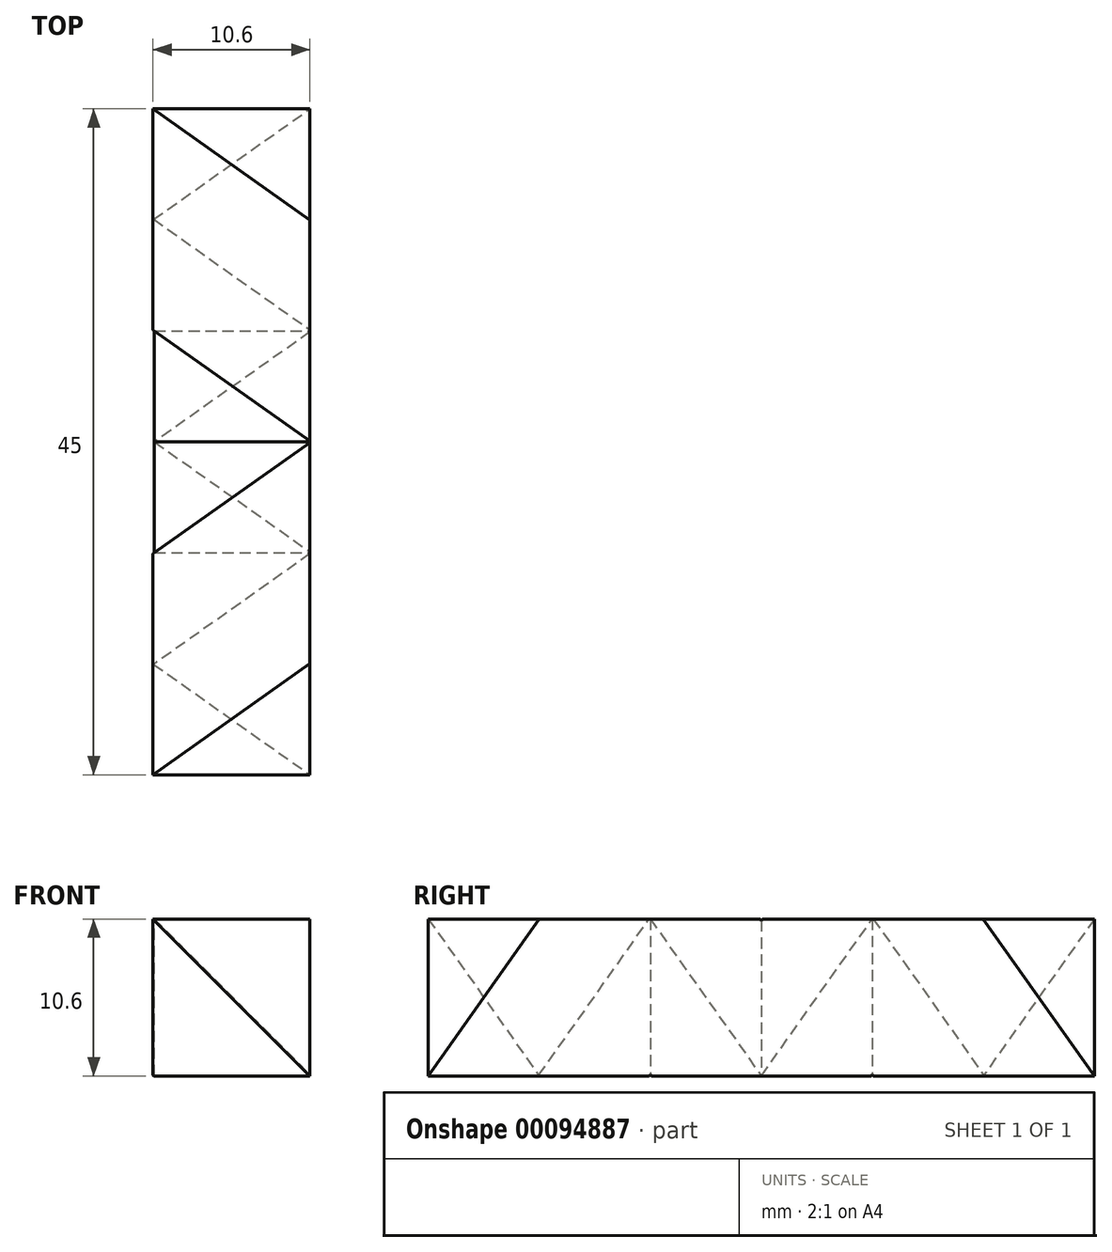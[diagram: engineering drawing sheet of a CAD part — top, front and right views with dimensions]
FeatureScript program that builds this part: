
annotation { "Feature Type Name" : "Feature", "Feature Type Description" : "" }
export const myFeature = defineFeature(function(context is Context, id is Id, definition is map)
    precondition{}
    {
        {
            var Q0;
            Q0=qCreatedBy(makeId("Front.planeOp"),FACE);
            var sketch = newSketch(context, id + "F0", { "sketchPlane" : qUnion([Q0])});
            skLineSegment(sketch, "E0.bottom", {"start": v(5.3, -5.3) * mm, "end": v(-5.3, -5.3) * mm});
            skLineSegment(sketch, "E0.top", {"start": v(5.3, 5.3) * mm, "end": v(-5.3, 5.3) * mm});
            skLineSegment(sketch, "E0.left", {"start": v(5.3, -5.3) * mm, "end": v(5.3, 5.3) * mm});
            skLineSegment(sketch, "E0.right", {"start": v(-5.3, -5.3) * mm, "end": v(-5.3, 5.3) * mm});
            skPoint(sketch, "E0.middle", {"position": v(0, 0) * mm});
            skSolve(sketch);
        }
        {
            var Q0;
            Q0=qSketchRegion(id+"F0",true);
            extrude(context, id + "F1", {"entities" : qUnion([Q0]), "depth" : 45 * mm, "symmetric" : true});
        }
        {
            var Q0;
            Q0=makeQuery(id+"F1.opExtrude","CAP_VERTEX",VERTEX,{"disambiguationData":[OSD([sQuery(id+"F0.wireOp",EDGE,"E0.top"),sQuery(id+"F0.wireOp",EDGE,"E0.left")])],"isStart":false});
            var Q1;
            Q1=makeQuery(id+"F1.opExtrude","CAP_VERTEX",VERTEX,{"disambiguationData":[OSD([sQuery(id+"F0.wireOp",EDGE,"E0.top"),sQuery(id+"F0.wireOp",EDGE,"E0.left")])],"isStart":true});
            var Q2;
            Q2=makeQuery(id+"F1.opExtrude","CAP_VERTEX",VERTEX,{"disambiguationData":[OSD([sQuery(id+"F0.wireOp",EDGE,"E0.bottom"),sQuery(id+"F0.wireOp",EDGE,"E0.right")])],"isStart":true});
            cPlane(context, id + "F2", {"entities" : qUnion([Q0, Q1, Q2]), "cplaneType" : CPlaneType.THREE_POINT, "offset" : 0 * mm, "width" : 150 * mm, "height" : 150 * mm});
        }
        {
            var Q0;
            Q0=qCreatedBy(id+"F2.planeOp",FACE);
            var sketch = newSketch(context, id + "F3", { "sketchPlane" : qUnion([Q0])});
            skLineSegment(sketch, "E1", {"start": v(22.5, 0) * mm, "end": v(15, 7.5) * mm});
            skLineSegment(sketch, "E2", {"start": v(15, -7.5) * mm, "end": v(22.5, 0) * mm});
            skLineSegment(sketch, "E3", {"start": v(15, 7.5) * mm, "end": v(15, 9.5) * mm});
            skLineSegment(sketch, "E4", {"start": v(15, 9.5) * mm, "end": v(24.5, 9.5) * mm});
            skLineSegment(sketch, "E5", {"start": v(24.5, 9.5) * mm, "end": v(24.5, -9.5) * mm});
            skLineSegment(sketch, "E6", {"start": v(24.5, -9.5) * mm, "end": v(15, -9.5) * mm});
            skLineSegment(sketch, "E7", {"start": v(15, -9.5) * mm, "end": v(15, -7.5) * mm});
            skLineSegment(sketch, "E8", {"start": v(0, 16.28) * mm, "end": v(0, -17.75) * mm, "construction": true});
            skLineSegment(sketch, "E9.MirrorCS", {"start": v(-22.5, 0) * mm, "end": v(-15, 7.5) * mm});
            skLineSegment(sketch, "E10.MirrorCS", {"start": v(-15, 7.5) * mm, "end": v(-15, 9.5) * mm});
            skLineSegment(sketch, "E11.MirrorCS", {"start": v(-15, 9.5) * mm, "end": v(-24.5, 9.5) * mm});
            skLineSegment(sketch, "E12.MirrorCS", {"start": v(-24.5, 9.5) * mm, "end": v(-24.5, -9.5) * mm});
            skLineSegment(sketch, "E13.MirrorCS", {"start": v(-24.5, -9.5) * mm, "end": v(-15, -9.5) * mm});
            skLineSegment(sketch, "E14.MirrorCS", {"start": v(-15, -9.5) * mm, "end": v(-15, -7.5) * mm});
            skLineSegment(sketch, "E15.MirrorCS", {"start": v(-15, -7.5) * mm, "end": v(-22.5, 0) * mm});
            skSolve(sketch);
        }
        {
            var Q0;
            Q0=makeQuery(id+"F3.imprint","IMPRINT",FACE,{"disambiguationData":[TD([[makeQuery(id+"F3.imprint","IMPRINT",EDGE,{"derivedFrom":sQuery(id+"F3.wireOp",EDGE,"E9.MirrorCS")}),1.0]])]});
            var Q1;
            Q1=makeQuery(id+"F3.imprint","IMPRINT",FACE,{"disambiguationData":[TD([[makeQuery(id+"F3.imprint","IMPRINT",EDGE,{"derivedFrom":sQuery(id+"F3.wireOp",EDGE,"E1")}),-1.0]])]});
            extrude(context, id + "F4", {"entities" : qUnion([Q0, Q1]), "operationType" : NewBodyOperationType.REMOVE, "oppositeDirection" : true, "depth" : 30 * mm, "symmetric" : true});
        }
        {
            var Q0;
            Q0=qCreatedBy(id+"F2.planeOp",FACE);
            var sketch = newSketch(context, id + "F5", { "sketchPlane" : qUnion([Q0])});
            skLineSegment(sketch, "E16", {"start": v(0, -22.47) * mm, "end": v(0, 25.47) * mm, "construction": true});
            skLineSegment(sketch, "E17", {"start": v(0, -7.5) * mm, "end": v(-7.5, 0) * mm});
            skLineSegment(sketch, "E18", {"start": v(-7.5, 0) * mm, "end": v(-15, -7.5) * mm});
            skLineSegment(sketch, "E19", {"start": v(-15, -7.5) * mm, "end": v(-15, -9.5) * mm});
            skLineSegment(sketch, "E20", {"start": v(-7.5, -14.21) * mm, "end": v(-7.5, 5.7) * mm, "construction": true});
            skLineSegment(sketch, "E21", {"start": v(0, -7.5) * mm, "end": v(7.5, 0) * mm});
            skLineSegment(sketch, "E22", {"start": v(7.5, 0) * mm, "end": v(15, -7.5) * mm});
            skLineSegment(sketch, "E23", {"start": v(15, -7.5) * mm, "end": v(15, -9.5) * mm});
            skLineSegment(sketch, "E24", {"start": v(-15, -9.5) * mm, "end": v(15, -9.5) * mm});
            skLineSegment(sketch, "E25", {"start": v(7.5, -14.16) * mm, "end": v(7.5, 5.45) * mm, "construction": true});
            skSolve(sketch);
        }
        {
            var Q0;
            Q0=makeQuery(id+"F5.imprint","IMPRINT",FACE,{"disambiguationData":[TD([[makeQuery(id+"F5.imprint","IMPRINT",EDGE,{"derivedFrom":sQuery(id+"F5.wireOp",EDGE,"E17")}),1.0]])]});
            var Q1;
            Q1=makeQuery(id+"F5.imprint","IMPRINT",FACE,{"disambiguationData":[TD([[makeQuery(id+"F5.imprint","IMPRINT",EDGE,{"derivedFrom":sQuery(id+"F5.wireOp",EDGE,"fdc7fff6-2170-4d3c-9e52-04dbe153ffdc0.MirrorCS")}),-1.0]])]});
            extrude(context, id + "F6", {"entities" : qUnion([Q0, Q1]), "operationType" : NewBodyOperationType.REMOVE, "depth" : 30 * mm, "symmetric" : true});
        }
        {
            var Q0;
            Q0=makeQuery(id+"F1.opExtrude","CAP_VERTEX",VERTEX,{"disambiguationData":[OSD([sQuery(id+"F0.wireOp",EDGE,"E0.top"),sQuery(id+"F0.wireOp",EDGE,"E0.right")])],"isStart":true});
            var Q1;
            Q1=makeQuery(id+"F1.opExtrude","CAP_VERTEX",VERTEX,{"disambiguationData":[OSD([sQuery(id+"F0.wireOp",EDGE,"E0.top"),sQuery(id+"F0.wireOp",EDGE,"E0.right")])],"isStart":false});
            var Q2;
            Q2=makeQuery(id+"F1.opExtrude","CAP_VERTEX",VERTEX,{"disambiguationData":[OSD([sQuery(id+"F0.wireOp",EDGE,"E0.bottom"),sQuery(id+"F0.wireOp",EDGE,"E0.left")])],"isStart":false});
            cPlane(context, id + "F7", {"entities" : qUnion([Q0, Q1, Q2]), "cplaneType" : CPlaneType.THREE_POINT, "offset" : 150 * mm, "width" : 150 * mm, "height" : 150 * mm});
        }
        {
            var Q0;
            Q0=qCreatedBy(id+"F7.planeOp",FACE);
            var sketch = newSketch(context, id + "F8", { "sketchPlane" : qUnion([Q0])});
            skLineSegment(sketch, "E26", {"start": v(0, 0) * mm, "end": v(-7.5, 7.5) * mm});
            skLineSegment(sketch, "E27", {"start": v(-7.5, 7.5) * mm, "end": v(-7.5, 9.5) * mm});
            skLineSegment(sketch, "E28", {"start": v(-7.5, 9.5) * mm, "end": v(7.5, 9.5) * mm});
            skLineSegment(sketch, "E29", {"start": v(7.5, 9.5) * mm, "end": v(7.5, 7.5) * mm});
            skLineSegment(sketch, "E30", {"start": v(7.5, 7.5) * mm, "end": v(0, 0) * mm});
            skSolve(sketch);
        }
        {
            var Q0;
            Q0=makeQuery(id+"F8.imprint","IMPRINT",FACE,{"disambiguationData":[TD([[makeQuery(id+"F8.imprint","IMPRINT",EDGE,{"derivedFrom":sQuery(id+"F8.wireOp",EDGE,"E26")}),-1.0]])]});
            extrude(context, id + "F9", {"entities" : qUnion([Q0]), "operationType" : NewBodyOperationType.REMOVE, "oppositeDirection" : true, "depth" : 30 * mm, "symmetric" : true});
        }
        {
            var Q0;
            Q0=qCreatedBy(id+"F2.planeOp",FACE);
            var sketch = newSketch(context, id + "F10", { "sketchPlane" : qUnion([Q0])});
            skLineSegment(sketch, "E31", {"start": v(17.07, -9.5) * mm, "end": v(7.5, 0.07) * mm});
            skLineSegment(sketch, "E32", {"start": v(7.5, 0.07) * mm, "end": v(0, -7.43) * mm});
            skLineSegment(sketch, "E33", {"start": v(0, -7.43) * mm, "end": v(-7.5, 0.07) * mm});
            skLineSegment(sketch, "E34", {"start": v(-7.5, 0.07) * mm, "end": v(-17.07, -9.5) * mm});
            skLineSegment(sketch, "E35", {"start": v(17.07, -9.5) * mm, "end": v(-17.07, -9.5) * mm});
            skSolve(sketch);
        }
        {
            var Q0;
            Q0 = qSketchRegion(id + "F10", true);
            extrude(context, id + "F11", {"entities" : qUnion([Q0]), "operationType" : NewBodyOperationType.REMOVE, "oppositeDirection" : true, "depth" : 30 * mm, "symmetric" : true});
        }
        {
            var Q0;
            Q0=qCreatedBy(id+"F7.planeOp",FACE);
            var sketch = newSketch(context, id + "F12", { "sketchPlane" : qUnion([Q0])});
            skLineSegment(sketch, "E36", {"start": v(-9.57, 9.5) * mm, "end": v(0, -0.07) * mm});
            skLineSegment(sketch, "E37", {"start": v(0, -0.07) * mm, "end": v(9.57, 9.5) * mm});
            skLineSegment(sketch, "E38", {"start": v(9.57, 9.5) * mm, "end": v(-9.57, 9.5) * mm});
            skSolve(sketch);
        }
        {
            var Q0;
            Q0 = qSketchRegion(id + "F12", true);
            extrude(context, id + "F13", {"entities" : qUnion([Q0]), "operationType" : NewBodyOperationType.REMOVE, "oppositeDirection" : true, "depth" : 30 * mm, "symmetric" : true});
        }
    });
